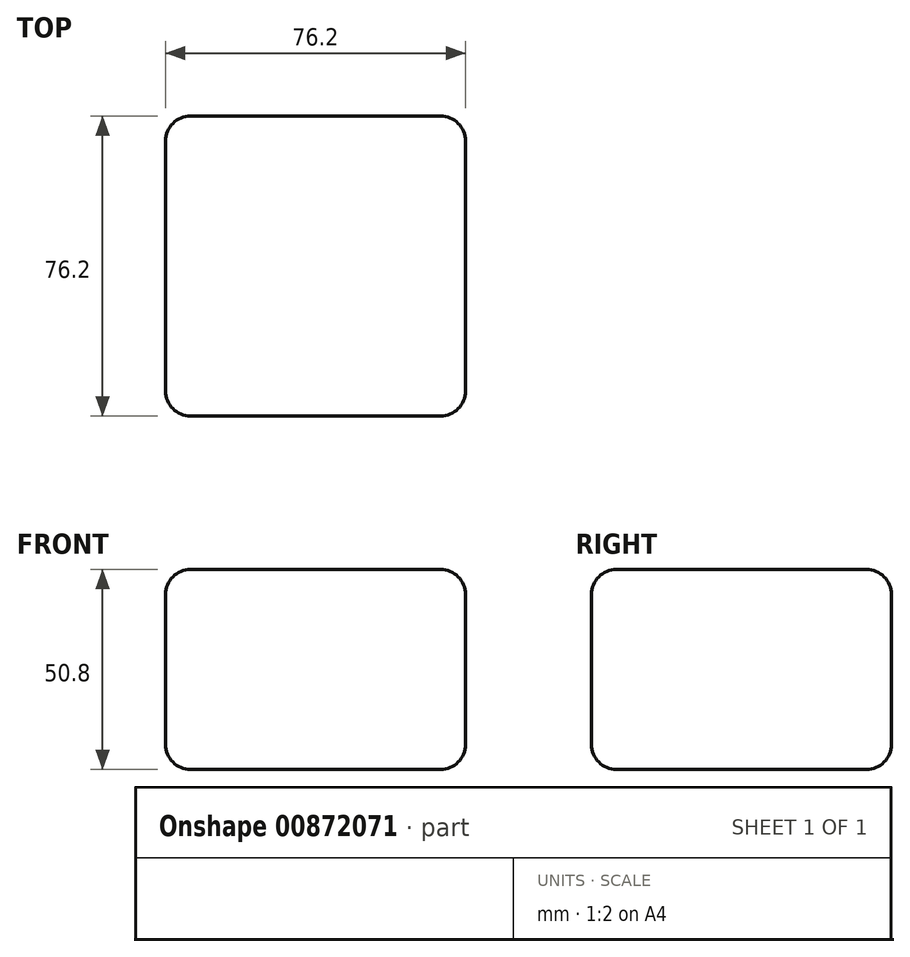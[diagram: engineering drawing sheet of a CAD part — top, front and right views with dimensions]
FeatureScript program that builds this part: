
annotation { "Feature Type Name" : "Feature", "Feature Type Description" : "" }
export const myFeature = defineFeature(function(context is Context, id is Id, definition is map)
    precondition{}
    {
        {
            var Q0;
            Q0=qCreatedBy(makeId("Front.planeOp"),FACE);
            var sketch = newSketch(context, id + "F0", { "sketchPlane" : qUnion([Q0])});
            skLineSegment(sketch, "E0.bottom", {"start": v(0, 0) * mm, "end": v(76.2, 0) * mm});
            skLineSegment(sketch, "E0.top", {"start": v(0, 50.8) * mm, "end": v(76.2, 50.8) * mm});
            skLineSegment(sketch, "E0.left", {"start": v(0, 0) * mm, "end": v(0, 50.8) * mm});
            skLineSegment(sketch, "E0.right", {"start": v(76.2, 0) * mm, "end": v(76.2, 50.8) * mm});
            skSolve(sketch);
        }
        {
            var Q0;
            Q0=makeQuery(id+"F0.imprint","IMPRINT",FACE,{"disambiguationData":[TD([[makeQuery(id+"F0.imprint","IMPRINT",EDGE,{"derivedFrom":sQuery(id+"F0.wireOp",EDGE,"E0.bottom")}),1.0]])]});
            extrude(context, id + "F1", {"entities" : qUnion([Q0]), "depth" : 76.2 * mm, "offsetDistance" : 25.4 * mm});
        }
        {
            var Q0;
            Q0=makeQuery(id+"F1.opExtrude","CAP_EDGE",EDGE,{"disambiguationData":[OSD([sQuery(id+"F0.wireOp",EDGE,"E0.top")])],"isStart":false});
            var Q1;
            Q1=makeQuery(id+"F1.opExtrude","SWEPT_EDGE",EDGE,{"disambiguationData":[OSD([sQuery(id+"F0.wireOp",EDGE,"E0.top"),sQuery(id+"F0.wireOp",EDGE,"E0.right")])]});
            var Q2;
            Q2=makeQuery(id+"F1.opExtrude","CAP_EDGE",EDGE,{"disambiguationData":[OSD([sQuery(id+"F0.wireOp",EDGE,"E0.right")])],"isStart":false});
            var Q3;
            Q3=makeQuery(id+"F1.opExtrude","CAP_EDGE",EDGE,{"disambiguationData":[OSD([sQuery(id+"F0.wireOp",EDGE,"E0.top")])],"isStart":true});
            var Q4;
            Q4=makeQuery(id+"F1.opExtrude","SWEPT_FACE",FACE,{"disambiguationData":[OSD([sQuery(id+"F0.wireOp",EDGE,"E0.top")])]});
            var Q5;
            Q5=makeQuery(id+"F1.opExtrude","CAP_FACE",FACE,{"disambiguationData":[OSD([sQuery(id+"F0.wireOp",EDGE,"E0.bottom"),sQuery(id+"F0.wireOp",EDGE,"E0.top"),sQuery(id+"F0.wireOp",EDGE,"E0.left"),sQuery(id+"F0.wireOp",EDGE,"E0.right")])],"isStart":false});
            var Q6;
            Q6=makeQuery(id+"F1.opExtrude","SWEPT_EDGE",EDGE,{"disambiguationData":[OSD([sQuery(id+"F0.wireOp",EDGE,"E0.bottom"),sQuery(id+"F0.wireOp",EDGE,"E0.left")])]});
            var Q7;
            Q7=makeQuery(id+"F1.opExtrude","CAP_EDGE",EDGE,{"disambiguationData":[OSD([sQuery(id+"F0.wireOp",EDGE,"E0.bottom")])],"isStart":true});
            var Q8;
            Q8=makeQuery(id+"F1.opExtrude","CAP_EDGE",EDGE,{"disambiguationData":[OSD([sQuery(id+"F0.wireOp",EDGE,"E0.left")])],"isStart":true});
            var Q9;
            Q9=makeQuery(id+"F1.opExtrude","SWEPT_FACE",FACE,{"disambiguationData":[OSD([sQuery(id+"F0.wireOp",EDGE,"E0.right")])]});
            fillet(context, id + "F2", {"entities" : qUnion([Q0, Q1, Q2, Q3, Q4, Q5, Q6, Q7, Q8, Q9]), "radius" : 6.35 * mm, "tangentPropagation" : true, "allowEdgeOverflow" : false});
        }
    });
